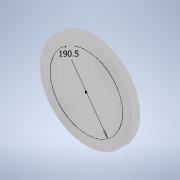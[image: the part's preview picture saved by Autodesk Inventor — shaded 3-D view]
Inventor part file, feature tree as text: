
AUTODESK INVENTOR PART (.ipt)
format: ipt  version: 2020 (Build 240168000, 168)  size: 393,728 bytes
history: native  units: in
note: dims shown in document units (in); Inventor stores cm internally (conversion verified against a paired STEP export)
features: other x2, sketch x1
ambient origin geometry x8: Origin, YZ Plane, XZ Plane, XY Plane, X Axis, Y Axis, Z Axis, Center Point
feature tree (3):
  other  "HTD5_152th_raw"
  sketch  "Sketch1"  dims[d0=7.5in]
  other  "MeshFeature1"
